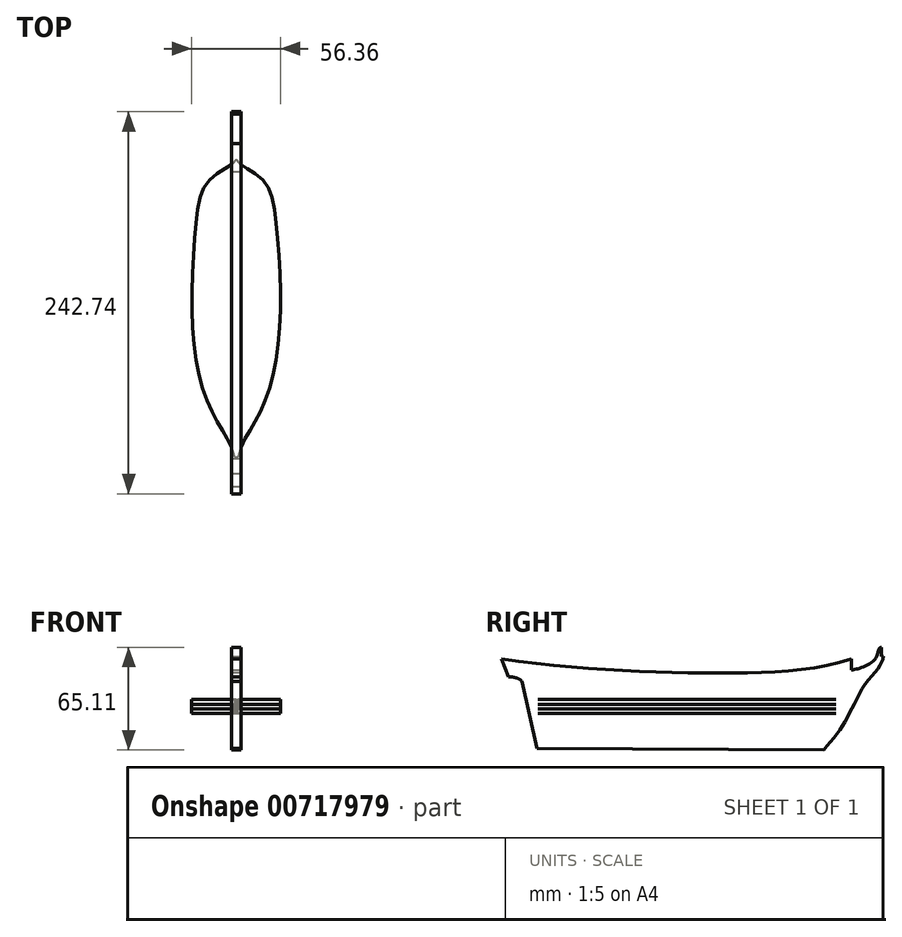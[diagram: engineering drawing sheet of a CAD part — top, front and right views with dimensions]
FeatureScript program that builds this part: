
annotation { "Feature Type Name" : "Feature", "Feature Type Description" : "" }
export const myFeature = defineFeature(function(context is Context, id is Id, definition is map)
    precondition{}
    {
        {
            var Q0;
            Q0=qCreatedBy(makeId("Right.planeOp"),FACE);
            var sketch = newSketch(context, id + "F0", { "sketchPlane" : qUnion([Q0])});
            skFitSpline(sketch, "E0", {"points": [v(-153.05, 17.45) * mm, v(-146.72, 16.21) * mm, v(-144.7, 14.3) * mm], "startDerivative": vector(12.12, -1.2) * mm, "endDerivative": vector(4.03, -5.36) * mm});
            skLineSegment(sketch, "E1", {"start": v(-144.7, 14.3) * mm, "end": v(-135.06, -28.02) * mm});
            skLineSegment(sketch, "E2", {"start": v(-135.06, -28.02) * mm, "end": v(47.04, -29.02) * mm});
            skFitSpline(sketch, "E3", {"points": [v(47.04, -29.02) * mm, v(57.2, -16.42) * mm, v(64.56, -3.42) * mm, v(73.52, 12.84) * mm, v(82.56, 24.17) * mm, v(85.1, 30.28) * mm], "startDerivative": vector(49.93, 57.8) * mm, "endDerivative": vector(12.5, 42.58) * mm});
            skLineSegment(sketch, "E4", {"start": v(85.1, 30.28) * mm, "end": v(83.71, 30.28) * mm});
            skLineSegment(sketch, "E5", {"start": v(83.71, 30.28) * mm, "end": v(83.71, 36.09) * mm});
            skFitSpline(sketch, "E6", {"points": [v(83.71, 36.09) * mm, v(82.48, 35.58) * mm, v(80.35, 29.59) * mm, v(71.27, 23.3) * mm, v(64.7, 21.74) * mm], "startDerivative": vector(-11.36, -0.97) * mm, "endDerivative": vector(-22.37, -3.66) * mm});
            skFitSpline(sketch, "E7", {"points": [v(64.7, 21.74) * mm, v(64.7, 28.69) * mm], "startDerivative": vector(0, 6.95) * mm, "endDerivative": vector(0, 6.95) * mm});
            skFitSpline(sketch, "E8", {"points": [v(64.7, 28.69) * mm, v(-22.1, 19.8) * mm, v(-157.65, 28.69) * mm], "startDerivative": vector(-178.29, -56.35) * mm, "endDerivative": vector(-256, 37.89) * mm});
            skLineSegment(sketch, "E9", {"start": v(-157.65, 28.69) * mm, "end": v(-153.05, 17.45) * mm});
            skSolve(sketch);
        }
        {
            var Q0;
            Q0=makeQuery(id+"F0.imprint","IMPRINT",FACE,{"disambiguationData":[TD([[makeQuery(id+"F0.imprint","IMPRINT",EDGE,{"derivedFrom":sQuery(id+"F0.wireOp",EDGE,"E0")}),1.0]])]});
            extrude(context, id + "F1", {"entities" : qUnion([Q0]), "endBound" : BoundingType.SYMMETRIC, "oppositeDirection" : true, "depth" : 6 * mm, "offsetDistance" : 25 * mm});
        }
        {
            var Q0;
            Q0=qCreatedBy(makeId("Top.planeOp"),FACE);
            var sketch = newSketch(context, id + "F2", { "sketchPlane" : qUnion([Q0])});
            skLineSegment(sketch, "E10", {"start": v(0, 75.9) * mm, "end": v(0, -190.07) * mm, "construction": true});
            skFitSpline(sketch, "E11", {"points": [v(0, 54.74) * mm, v(-4.03, 50.89) * mm, v(-17.99, 40.52) * mm, v(-25.22, 16.42) * mm, v(-28.04, -43.63) * mm, v(-20.76, -92.06) * mm, v(-9.38, -116.42) * mm, v(-1.08, -134.33) * mm], "startDerivative": vector(-40.98, -53.46) * mm, "endDerivative": vector(40.14, -182.25) * mm});
            skLineSegment(sketch, "E12", {"start": v(-1.08, -134.33) * mm, "end": v(0, -134.33) * mm});
            skLineSegment(sketch, "E13.MirrorCS", {"start": v(1.08, -134.33) * mm, "end": v(0, -134.33) * mm});
            skFitSpline(sketch, "E14.MirrorCS", {"points": [v(0, 54.74) * mm, v(4.03, 50.89) * mm, v(17.99, 40.52) * mm, v(25.22, 16.42) * mm, v(28.04, -43.63) * mm, v(20.76, -92.06) * mm, v(9.38, -116.42) * mm, v(1.08, -134.33) * mm], "startDerivative": vector(40.98, -53.46) * mm, "endDerivative": vector(-40.14, -182.25) * mm});
            skFitSpline(sketch, "E15", {"points": [v(-0.82, 60.57) * mm, v(-8.52, 58.02) * mm, v(-16.92, 53.95) * mm, v(-23.41, 47.2) * mm, v(-24.85, 43.79) * mm, v(-27.41, 30.54) * mm, v(-29.38, 7.4) * mm, v(-30.17, -24.48) * mm, v(-29.97, -34.32) * mm, v(-29.5, -60.94) * mm, v(-25.14, -102.57) * mm, v(-18.57, -124.66) * mm, v(-13.19, -136.45) * mm, v(-10.97, -138.76) * mm, v(-6.3, -139.26) * mm, v(0, -139.4) * mm], "startDerivative": vector(-146.26, -47.03) * mm, "endDerivative": vector(145.75, -13.85) * mm});
            skFitSpline(sketch, "E16.MirrorCS", {"points": [v(0.82, 60.57) * mm, v(8.52, 58.02) * mm, v(16.92, 53.95) * mm, v(23.41, 47.2) * mm, v(24.85, 43.79) * mm, v(27.41, 30.54) * mm, v(29.38, 7.4) * mm, v(30.17, -24.48) * mm, v(29.97, -34.32) * mm, v(29.5, -60.94) * mm, v(25.14, -102.57) * mm, v(18.57, -124.66) * mm, v(13.19, -136.45) * mm, v(10.97, -138.76) * mm, v(6.3, -139.26) * mm, v(0, -139.4) * mm], "startDerivative": vector(146.26, -47.03) * mm, "endDerivative": vector(-145.75, -13.85) * mm});
            skSolve(sketch);
        }
        {
            var Q0;
            Q0=makeQuery(id+"F2.imprint","IMPRINT",FACE,{"disambiguationData":[TD([[makeQuery(id+"F2.imprint","IMPRINT",EDGE,{"derivedFrom":sQuery(id+"F2.wireOp",EDGE,"E11")}),1.0]])]});
            extrude(context, id + "F3", {"entities" : qUnion([Q0]), "endBound" : BoundingType.SYMMETRIC, "depth" : 6 * mm, "offsetDistance" : 25 * mm});
        }
        {
            var Q0;
            Q0 = qSketchRegion(id + "F2", true);
            extrude(context, id + "F4", {"entities" : qUnion([Q0]), "oppositeDirection" : true, "depth" : 6 * mm, "offsetDistance" : 25 * mm});
        }
    });
